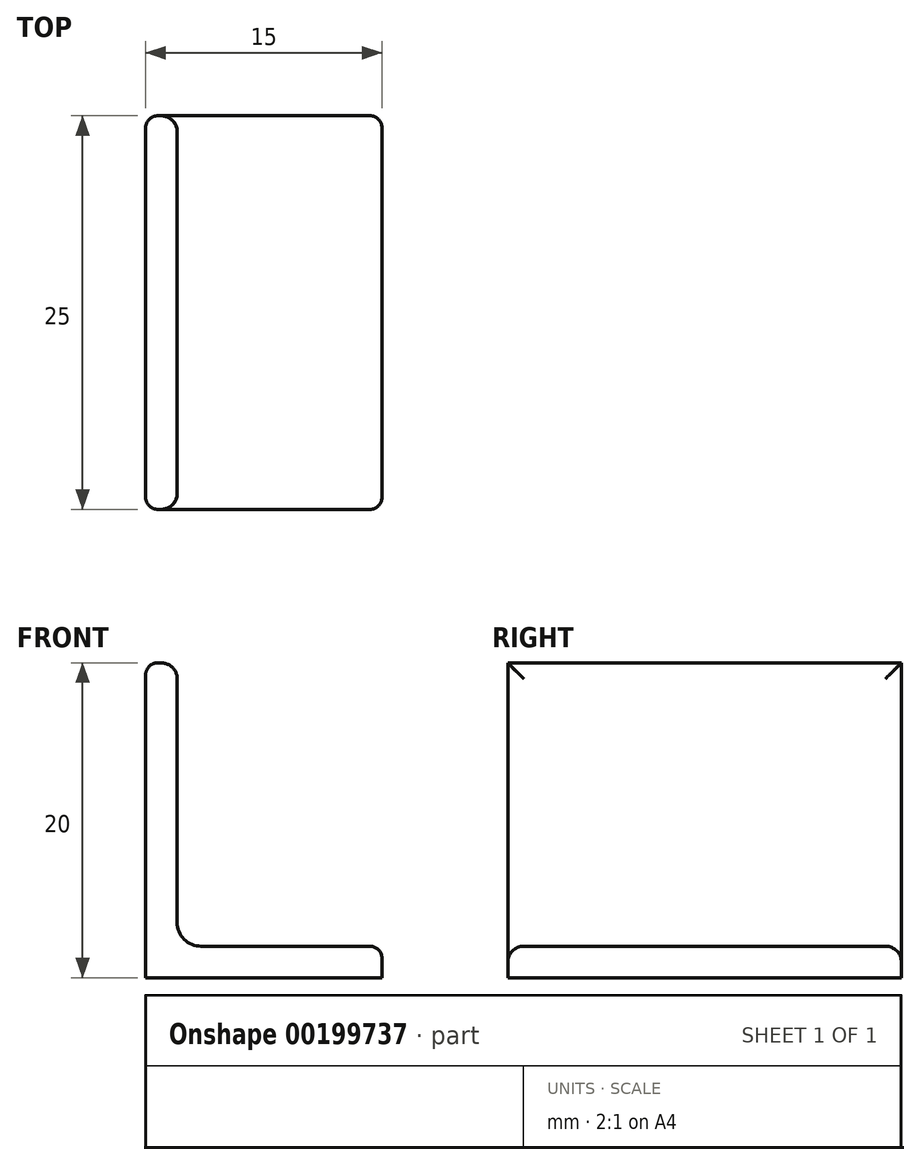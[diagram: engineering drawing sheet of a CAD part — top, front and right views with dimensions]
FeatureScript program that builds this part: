
annotation { "Feature Type Name" : "Feature", "Feature Type Description" : "" }
export const myFeature = defineFeature(function(context is Context, id is Id, definition is map)
    precondition{}
    {
        {
            var Q0;
            Q0=qCreatedBy(makeId("Front.planeOp"),FACE);
            var sketch = newSketch(context, id + "F0", { "sketchPlane" : qUnion([Q0])});
            skLineSegment(sketch, "E0", {"start": v(0, 0) * mm, "end": v(-15, 0) * mm});
            skLineSegment(sketch, "E1", {"start": v(-15, 0) * mm, "end": v(-15, 20) * mm});
            skLineSegment(sketch, "E2", {"start": v(-15, 20) * mm, "end": v(-13, 20) * mm});
            skLineSegment(sketch, "E3", {"start": v(-13, 20) * mm, "end": v(-13, 3.52) * mm});
            skLineSegment(sketch, "E4", {"start": v(-11.48, 2) * mm, "end": v(0, 2) * mm});
            skLineSegment(sketch, "E5", {"start": v(0, 2) * mm, "end": v(0, 0) * mm});
            skPoint(sketch, "E6.visualSharp", {"position": v(-13, 2) * mm});
            skArc(sketch, "E6.filletArc", {"start": v(-13, 3.52) * mm, "mid": v(-12.55, 2.45) * mm, "end": v(-11.48, 2) * mm});
            skSolve(sketch);
        }
        {
            var Q0;
            Q0 = qSketchRegion(id + "F0", true);
            extrude(context, id + "F1", {"entities" : qUnion([Q0]), "depth" : 25 * mm});
        }
        {
            var Q0;
            Q0=makeQuery(id+"F1.opExtrude","SWEPT_FACE",FACE,{"disambiguationData":[OSD([sQuery(id+"F0.wireOp",EDGE,"E3")])]});
            fillet(context, id + "F2", {"entities" : qUnion([Q0]), "radius" : 1.02 * mm, "tangentPropagation" : true, "allowEdgeOverflow" : false});
        }
        {
            var Q0;
            Q0=makeQuery(id+"F1.opExtrude","CAP_EDGE",EDGE,{"disambiguationData":[OSD([sQuery(id+"F0.wireOp",EDGE,"E1")])],"isStart":true});
            var Q1;
            Q1=makeQuery(id+"F1.opExtrude","SWEPT_EDGE",EDGE,{"disambiguationData":[OSD([sQuery(id+"F0.wireOp",EDGE,"E1"),sQuery(id+"F0.wireOp",EDGE,"E2")])]});
            var Q2;
            Q2=makeQuery(id+"F1.opExtrude","CAP_EDGE",EDGE,{"disambiguationData":[OSD([sQuery(id+"F0.wireOp",EDGE,"E1")])],"isStart":false});
            fillet(context, id + "F3", {"entities" : qUnion([Q0, Q1, Q2]), "radius" : .75 * mm, "tangentPropagation" : true, "allowEdgeOverflow" : false});
        }
        {
            var Q0;
            Q0=makeQuery(id+"F1.opExtrude","CAP_EDGE",EDGE,{"disambiguationData":[OSD([sQuery(id+"F0.wireOp",EDGE,"E5")])],"isStart":false});
            var Q1;
            Q1=makeQuery(id+"F2.opFillet","BLEND_EDGE",EDGE,{"blendedFrom":[makeQuery(id+"F1.opExtrude","CAP_EDGE",EDGE,{"disambiguationData":[OSD([sQuery(id+"F0.wireOp",EDGE,"E4")])],"isStart":false}),makeQuery(id+"F1.opExtrude","SWEPT_FACE",FACE,{"disambiguationData":[OSD([sQuery(id+"F0.wireOp",EDGE,"E5")])]})],"blendedInto":[makeQuery(id+"F1.opExtrude","SWEPT_FACE",FACE,{"disambiguationData":[OSD([sQuery(id+"F0.wireOp",EDGE,"E5")])]})]});
            var Q2;
            Q2=makeQuery(id+"F1.opExtrude","SWEPT_EDGE",EDGE,{"disambiguationData":[OSD([sQuery(id+"F0.wireOp",EDGE,"E4"),sQuery(id+"F0.wireOp",EDGE,"E5")])]});
            var Q3;
            Q3=makeQuery(id+"F2.opFillet","BLEND_EDGE",EDGE,{"blendedFrom":[makeQuery(id+"F1.opExtrude","CAP_EDGE",EDGE,{"disambiguationData":[OSD([sQuery(id+"F0.wireOp",EDGE,"E4")])],"isStart":true}),makeQuery(id+"F1.opExtrude","SWEPT_FACE",FACE,{"disambiguationData":[OSD([sQuery(id+"F0.wireOp",EDGE,"E5")])]})],"blendedInto":[makeQuery(id+"F1.opExtrude","SWEPT_FACE",FACE,{"disambiguationData":[OSD([sQuery(id+"F0.wireOp",EDGE,"E5")])]})]});
            var Q4;
            Q4=makeQuery(id+"F1.opExtrude","CAP_EDGE",EDGE,{"disambiguationData":[OSD([sQuery(id+"F0.wireOp",EDGE,"E5")])],"isStart":true});
            fillet(context, id + "F4", {"entities" : qUnion([Q0, Q1, Q2, Q3, Q4]), "radius" : 0.76 * mm, "tangentPropagation" : true, "allowEdgeOverflow" : false});
        }
    });
